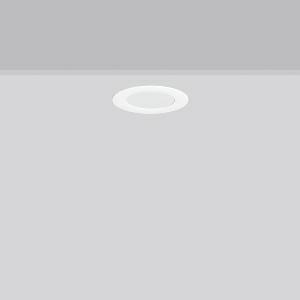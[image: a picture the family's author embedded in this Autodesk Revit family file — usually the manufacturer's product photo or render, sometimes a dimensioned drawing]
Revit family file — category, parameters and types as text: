
# Revit family: toledo_flat_round_e_901451_002_1_76_912b
name_source: partatom
category: Lighting Fixtures
units: mm (PartAtom-declared; Revit-internal decimal feet)

## family parameters
Cut with Voids When Loaded = No
Host = Face
Light Source = No
Part Type = Normal
Room Calculation Point = No
Round Connector Dimension = Use Diameter
Shared = No

## types (1)
- TOLEDO FLAT round E (1 x LED Modul 840, 530 lm, 4000)
    Apparent Load = 5 VA
    CIE Flux Codes = 48 79 96 100 100
    Color Rendering = 80
    Color Temperature = 4000
    Default Elevation = 1800 mm
    Description = Series: TOLEDO FLAT round
Ultra thin recessed downlight. Housing: die-cast aluminium. Light guide and diffuser made of non-yellowing PMMA, opal matt. Ceiling installation with spring system. Mounting depth depends on ceiling strength. Including separate LED converter with connecting cable 250 mm. Suitable for through-wiring with separately available accessories. Surface mounted housing as accessory for all sizes. Retrofittable decorative cylinders made of chintz fabric as accessory, optional with satin finish plastic diffuser. Through-wiring box (5 pole) available as accessory. 
Colour: white
Diameter: 148 mm
Height: 2 mm
Cut-out diameter: 128 mm
Recess height: 31-53 mm
Luminaire: recess height: 31-51 mm
Lamp: LED
Socket: without socket
Colour temperature: 4000K
Colour rendering index (CRI): 80
System power: 5 W
Rated luminous flux: 530 lm
Luminous efficiency: 106 lm/W
Control gear: Converter, dimmable, DALI
Protection class: II
Type of protection: IP 54
    Height = 0 mm  [stored 0 ft]
    Lamp = 1 x LED Modul 840
    Lamp Light Flux = 530 lm
    Lamp count = 1
    Length = 148 mm
    Lifetime = 50000 h
    Luminous efficacy = 106 lm/W
    Manufacturer = RZB
    ModVariant = No
    Model = 901451.002.1.76
    Mounting Place = Ceiling
    Mounting Type = Recessed
    Number of Poles = 1
    OnlyDefault = Yes
    Power Factor = 1
    Product Name = TOLEDO FLAT round E
    Product group = Recessed downlights
    ProductGroupID = 402
    Protection Class = Protection class II
    Protection Degree = IP 20
    RLX_Detail_Level = 1
    RLX_Emergency_Light_Flux = 0 lm
    RLX_Emergency_Type = 0
    RLX_Emergency_Type_DB = No
    RlxData = <blob elided: 75221 chars, md5=550f268c>
    Socket = socket
    Standby Power = 0 W
    System Light Flux = 530 lm
    System Power = 5 W
    Type Comments = Product without accessories
    Type Image = 901451.002.jpg
    URL = http://relux.com
    VarID = ---
    Voltage = 230 V
    Voltage Range = 220-240 V
    Weight = 0.00 kg
    Width = 0 mm  [stored 0 ft]

note: [stored X ft] marks values corroborated as IEEE doubles in the binary element streams (Revit-internal decimal feet)

## geometry (parser evidence)
native form markers: Blend x4, Sweep x11
no freeform markers — native parametric forms only
